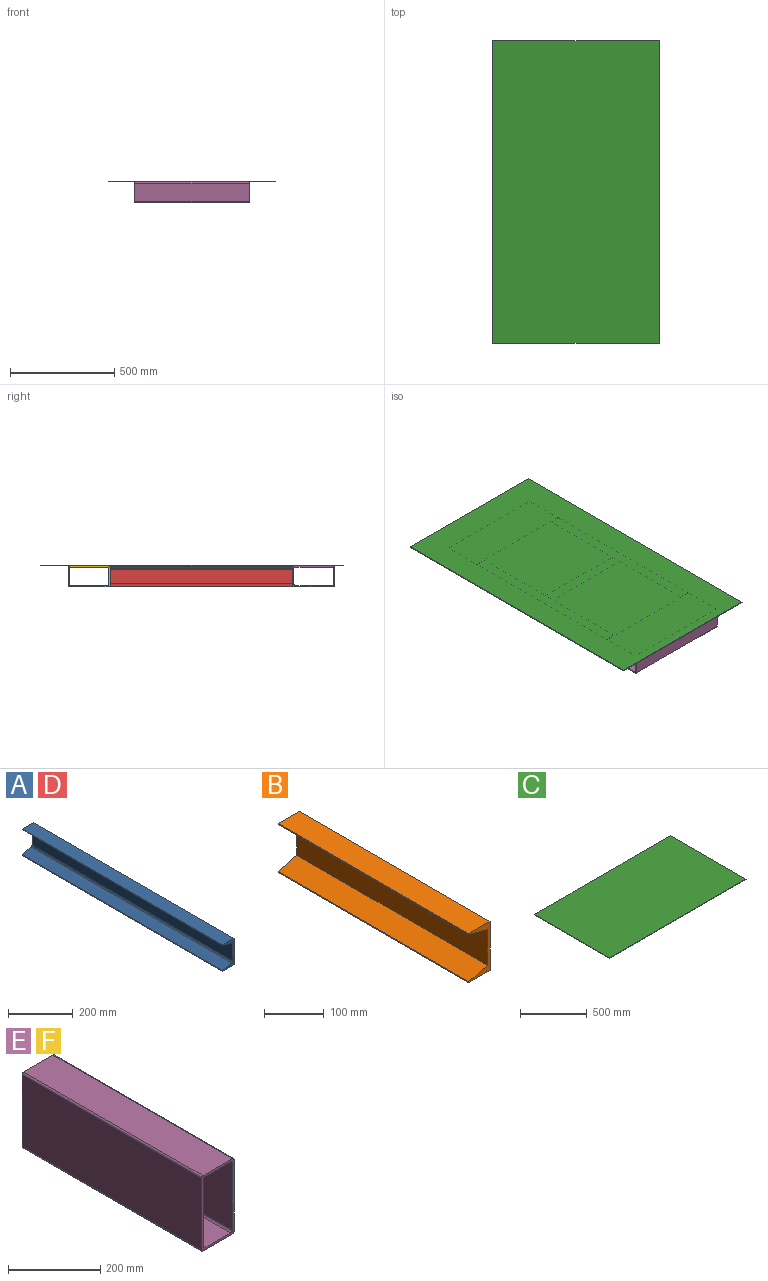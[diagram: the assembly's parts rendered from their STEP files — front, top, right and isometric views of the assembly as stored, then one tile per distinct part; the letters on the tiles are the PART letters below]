
ASSEMBLY  parts=6 mates=5
PART A: 14 faces, bbox 50x875x100 mm
  f0: plane 875x100mm, normal (1,0,0), area 87500mm2, adj f1,f4,f8,f9
  f1: plane 875x50mm, normal (0,0,1), area 43750mm2, adj f0,f2,f8,f9
  f2: plane 875x0.45mm, normal (-1,0,0), area 396.8mm2, adj f1,f8,f9,f12
  f3: plane 875x0.45mm, normal (-1,0,0), area 396.8mm2, adj f4,f8,f9,f13
  f4: plane 875x50mm, normal (0,0,-1), area 43750mm2, adj f0,f3,f8,f9
  f5: plane 875x38.76mm, normal (-0.25,0,-0.97), area 35043.9mm2, adj f8,f9,f10,f12
  f6: plane 875x65.39mm, normal (-1,0,0), area 57214.1mm2, adj f8,f9,f10,f11
  f7: plane 875x38.76mm, normal (-0.25,0,0.97), area 35043.9mm2, adj f8,f9,f11,f13
  f8: plane 100x50mm, normal (0,-1,0), area 1284.2mm2, adj f0,f1,f2,f3,f4,f5,f6,f7
  f9: plane 100x50mm, normal (0,1,0), area 1284.2mm2, adj f0,f1,f2,f3,f4,f5,f6,f7
  f10: cylinder r=5mm len=875mm, axis (0,1,0), area 5759.4mm2, adj f5,f6,f8,f9
  f11: cylinder r=5mm len=875mm, axis (0,-1,0), area 5759.4mm2, adj f6,f7,f8,f9
  f12: cylinder r=2mm len=875mm, axis (0,-1,0), area 2303.8mm2, adj f2,f5,f8,f9
  f13: cylinder r=2mm len=875mm, axis (0,-1,0), area 2303.8mm2, adj f3,f7,f8,f9
PART B: 10 faces, bbox 50x450x100 mm
  f0: plane 450x100mm, normal (1,0,0), area 45000mm2, adj f1,f7,f8,f9
  f1: plane 450x50mm, normal (0,0,1), area 22500mm2, adj f0,f2,f8,f9
  f2: plane 450x2mm, normal (-1,0,0), area 900mm2, adj f1,f3,f8,f9
  f3: plane 450x44mm, normal (-0.25,0,-0.97), area 20458.3mm2, adj f2,f4,f8,f9
  f4: plane 450x73.12mm, normal (-1,0,0), area 32904mm2, adj f3,f5,f8,f9
  f5: plane 450x44mm, normal (-0.25,0,0.97), area 20458.3mm2, adj f4,f6,f8,f9
  f6: plane 450x2mm, normal (-1,0,0), area 900mm2, adj f5,f7,f8,f9
  f7: plane 450x50mm, normal (0,0,-1), area 22500mm2, adj f0,f6,f8,f9
  f8: plane 100x50mm, normal (0,-1,0), area 1279.4mm2, adj f0,f1,f2,f3,f4,f5,f6,f7
  f9: plane 100x50mm, normal (0,1,0), area 1279.4mm2, adj f0,f1,f2,f3,f4,f5,f6,f7
PART C: 6 faces, bbox 1450x800x4 mm
  f0: plane 800x4mm, normal (1,0,0), area 3200mm2, adj f1,f3,f4,f5
  f1: plane 1450x4mm, normal (0,1,0), area 5800mm2, adj f0,f2,f4,f5
  f2: plane 800x4mm, normal (-1,0,0), area 3200mm2, adj f1,f3,f4,f5
  f3: plane 1450x4mm, normal (0,-1,0), area 5800mm2, adj f0,f2,f4,f5
  f4: plane 1450x800mm, normal (0,0,1), area 1160000mm2, adj f0,f1,f2,f3
  f5: plane 1450x800mm, normal (0,0,-1), area 1160000mm2, adj f0,f1,f2,f3
PART D: same geometry as A
PART E: 18 faces, bbox 100x550x200 mm
  f0: plane 550x90mm, normal (0,0,1), area 49500mm2, adj f8,f9,f14,f17
  f1: plane 550x190mm, normal (-1,0,0), area 104500mm2, adj f8,f9,f14,f15
  f2: plane 550x90mm, normal (0,0,-1), area 49500mm2, adj f8,f9,f15,f16
  f3: plane 550x178mm, normal (1,0,0), area 97900mm2, adj f8,f9,f10,f13
  f4: plane 550x78mm, normal (0,0,-1), area 42900mm2, adj f8,f9,f10,f11
  f5: plane 550x178mm, normal (-1,0,0), area 97900mm2, adj f8,f9,f11,f12
  f6: plane 550x78mm, normal (0,0,1), area 42900mm2, adj f8,f9,f12,f13
  f7: plane 550x190mm, normal (1,0,0), area 104500mm2, adj f8,f9,f16,f17
  f8: plane 200x100mm, normal (0,-1,0), area 3456mm2, adj f0,f1,f2,f3,f4,f5,f6,f7
  f9: plane 200x100mm, normal (0,1,0), area 3456mm2, adj f0,f1,f2,f3,f4,f5,f6,f7
  f10: cylinder r=5mm len=550mm, axis (0,1,0), area 4319.7mm2, adj f3,f4,f8,f9
  f11: cylinder r=5mm len=550mm, axis (0,-1,0), area 4319.7mm2, adj f4,f5,f8,f9
  f12: cylinder r=5mm len=550mm, axis (0,1,0), area 4319.7mm2, adj f5,f6,f8,f9
  f13: cylinder r=5mm len=550mm, axis (0,-1,0), area 4319.7mm2, adj f3,f6,f8,f9
  f14: cylinder r=5mm len=550mm, axis (0,-1,0), area 4319.7mm2, adj f0,f1,f8,f9
  f15: cylinder r=5mm len=550mm, axis (0,1,0), area 4319.7mm2, adj f1,f2,f8,f9
  f16: cylinder r=5mm len=550mm, axis (0,-1,0), area 4319.7mm2, adj f2,f7,f8,f9
  f17: cylinder r=5mm len=550mm, axis (0,1,0), area 4319.7mm2, adj f0,f7,f8,f9
PART F: same geometry as E
PLACE A rot(axis=(0,0,1),180deg) t=(-507.91,-1703.88,-345.42)mm
PLACE B rot(axis=(0,0,1),90deg) t=(-942.24,-1123.73,-290.42)mm
PLACE C rot(axis=(0.71,-0.71,0),180deg) t=(-717.24,-983.88,-386.54)mm fixed
PLACE D rot(axis=(1,0,0),180deg) t=(-926.57,-1703.88,-535.67)mm
PLACE E rot(axis=(-0.58,-0.58,-0.58),120deg) t=(-717.24,-1566.38,-440.54)mm
PLACE F rot(axis=(0.58,0.58,-0.58),120deg) t=(-717.24,-491.38,-440.54)mm
MATE fastened B.f1 <-> C.f4  axis (0,0,1) through (-717.24,-1028.88,-390.54)mm
MATE fastened E.f0 <-> D.f9  axis (0,1,0) through (-992.24,-1466.38,-440.54)mm
MATE fastened F.f0 <-> D.f8  axis (0,-1,0) through (-992.24,-591.38,-440.54)mm
MATE fastened D.f0 <-> B.f9  axis (1,0,0) through (-942.24,-1028.88,-440.54)mm
MATE fastened B.f8 <-> A.f0  axis (1,0,0) through (-492.24,-1003.88,-440.54)mm
